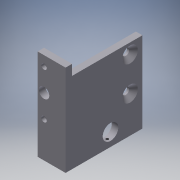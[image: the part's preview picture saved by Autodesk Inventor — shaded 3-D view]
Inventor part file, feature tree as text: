
AUTODESK INVENTOR PART (.ipt)
format: ipt  version: 2018 (Build 220112000, 112)  size: 187,392 bytes
history: native  units: mm
features: extrude x4, hole x3, reference x3, projected_geometry x2, sketch x1
ambient origin geometry x8: Origin, YZ Plane, XZ Plane, XY Plane, X Axis, Y Axis, Z Axis, Center Point
bodies: Volumenkörper1 (feature_tree)
feature tree (13):
  extrude  "Extrusion1"  Depth=8.0mm
  hole  "Bohrung1"  [1 undecoded]
  extrude  "Extrusion2"  Depth=8.0mm
  hole  "Bohrung2"  [1 undecoded]
  extrude  "Extrusion3"  Depth=8.0mm
  hole  "Bohrung3"  [1 undecoded]
  extrude  "Extrusion4"  Depth=8.0mm
  reference  "Referenz1"
  reference  "Referenz2"
  reference  "Referenz3"
  projected_geometry  "Projizierte Kontur1"
  sketch  "Skizze7"  dims[d0=16.5mm d1=5.0mm d2=5.0mm d3=54.0mm d4=70.0mm d5=0.0mm d6=35.0mm d7=5.0mm d8=5.0mm d9=7.5mm d10=4.2mm d11=6.0mm d12=9.0mm d13=2.0mm d14=90.0deg d15=8.0mm d16=20.594885mm d18=17.5mm d19=8.0mm d20=50.0mm d21=0.0mm d26=5.3mm d27=6.0mm d28=12.0mm d29=2.0mm d30=90.0deg d31=8.0mm d32=20.594885mm d34=9.5mm d35=9.5mm d36=16.0mm d37=26.0mm d38=24.5mm d39=12.0mm d40=10.0mm d41=5.0mm d42=0.0mm d43=2.013mm d44=6.0mm d45=4.0mm d46=2.0mm d47=90.0deg d48=8.0mm d49=20.594885mm d50=8.0mm d51=5.0mm d52=0.0mm]
  projected_geometry  "Projizierte Kontur2"
note: 3 required parameter values undecoded (feature->parameter linkage not recoverable at this tier; creation-order binding heuristic only, values carry confidence <= 0.55)
